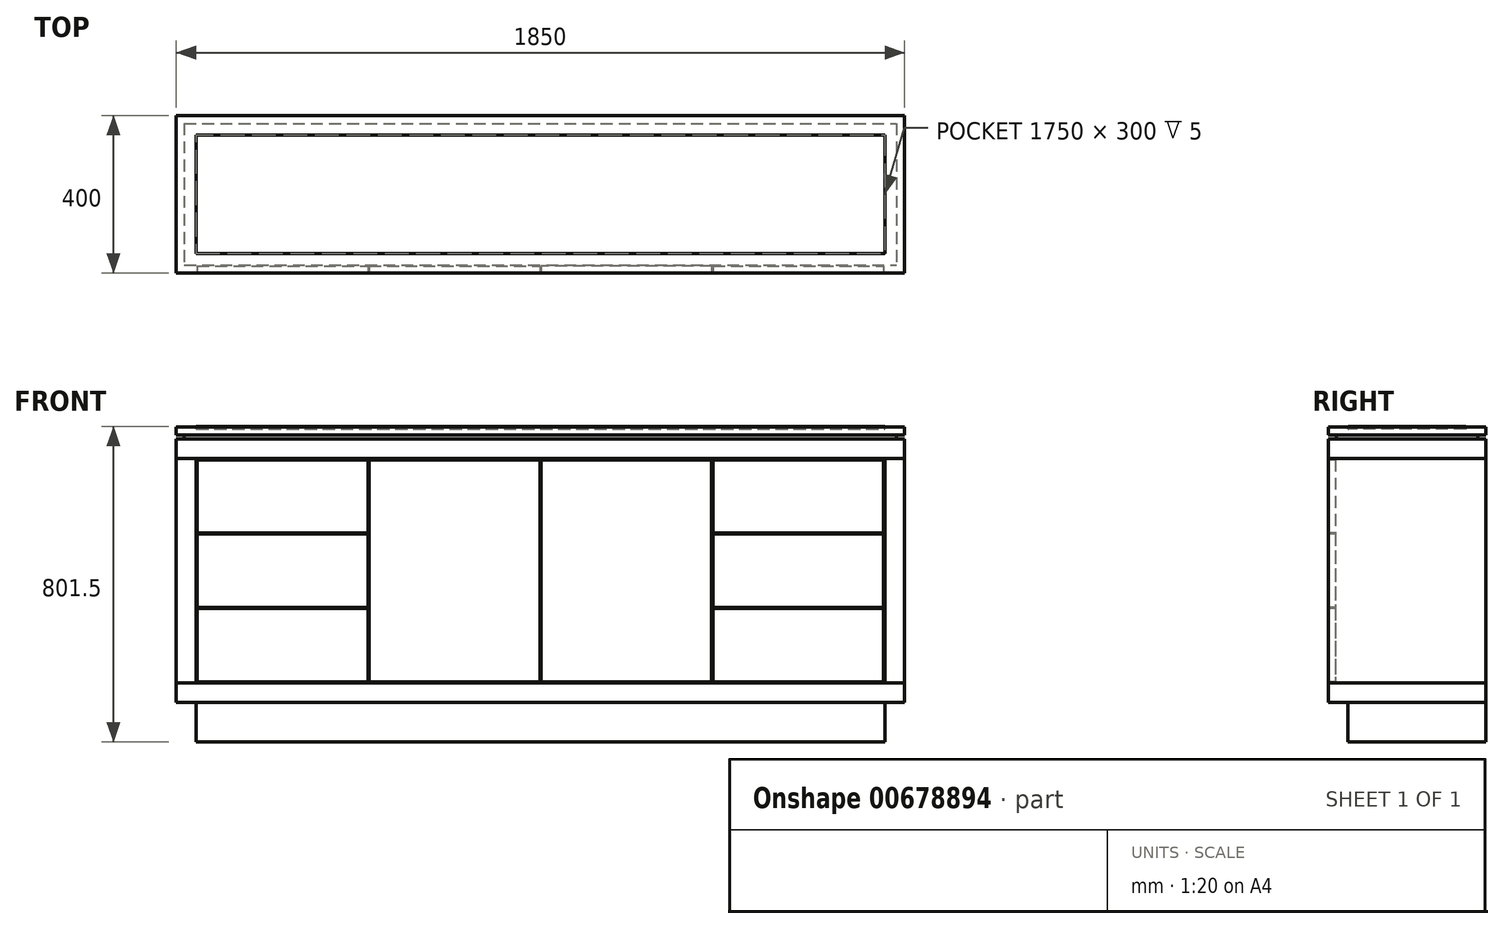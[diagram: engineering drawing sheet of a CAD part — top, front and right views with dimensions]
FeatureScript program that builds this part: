
annotation { "Feature Type Name" : "Feature", "Feature Type Description" : "" }
export const myFeature = defineFeature(function(context is Context, id is Id, definition is map)
    precondition{}
    {
        {
            var Q0;
            Q0=qCreatedBy(makeId("Front.planeOp"),FACE);
            var sketch = newSketch(context, id + "F0", { "sketchPlane" : qUnion([Q0])});
            skLineSegment(sketch, "E0.bottom", {"start": v(-925, 770) * mm, "end": v(925, 770) * mm});
            skLineSegment(sketch, "E0.top", {"start": v(-925, 100) * mm, "end": v(925, 100) * mm});
            skLineSegment(sketch, "E0.left", {"start": v(-925, 770) * mm, "end": v(-925, 100) * mm});
            skLineSegment(sketch, "E1.bottom", {"start": v(-925, 800) * mm, "end": v(925, 800) * mm});
            skLineSegment(sketch, "E1.top", {"start": v(-925, 780) * mm, "end": v(925, 780) * mm});
            skLineSegment(sketch, "E1.left", {"start": v(-925, 800) * mm, "end": v(-925, 780) * mm});
            skLineSegment(sketch, "E1.right", {"start": v(925, 800) * mm, "end": v(925, 780) * mm});
            skLineSegment(sketch, "E2", {"start": v(-875, 100) * mm, "end": v(-875, 0) * mm});
            skLineSegment(sketch, "E3", {"start": v(-875, 0) * mm, "end": v(875, 0) * mm});
            skLineSegment(sketch, "E4", {"start": v(875, 0) * mm, "end": v(875, 100) * mm});
            skLineSegment(sketch, "E5", {"start": v(905, 780) * mm, "end": v(905, 770) * mm});
            skLineSegment(sketch, "E6", {"start": v(925, 780) * mm, "end": v(925, 770) * mm, "construction": true});
            skLineSegment(sketch, "E7", {"start": v(-925, 780) * mm, "end": v(-925, 770) * mm, "construction": true});
            skLineSegment(sketch, "E8", {"start": v(-905, 770) * mm, "end": v(-905, 780) * mm});
            skLineSegment(sketch, "E9", {"start": v(925, 770) * mm, "end": v(925, 100) * mm});
            skLineSegment(sketch, "E10", {"start": v(925, 100) * mm, "end": v(925, 0) * mm, "construction": true});
            skLineSegment(sketch, "E11", {"start": v(925, 0) * mm, "end": v(875, 0) * mm, "construction": true});
            skLineSegment(sketch, "E12", {"start": v(-925, 100) * mm, "end": v(-925, 0) * mm, "construction": true});
            skLineSegment(sketch, "E13", {"start": v(-925, 0) * mm, "end": v(-875, 0) * mm, "construction": true});
            skLineSegment(sketch, "E14", {"start": v(-905, 775) * mm, "end": v(-925, 775) * mm, "construction": true});
            skLineSegment(sketch, "E15", {"start": v(925, 775) * mm, "end": v(905, 775) * mm, "construction": true});
            skLineSegment(sketch, "E16", {"start": v(-925, 720) * mm, "end": v(925, 720) * mm});
            skLineSegment(sketch, "E17", {"start": v(-925, 150) * mm, "end": v(925, 150) * mm});
            skLineSegment(sketch, "E18", {"start": v(-875, 100) * mm, "end": v(-875, 770) * mm});
            skLineSegment(sketch, "E19", {"start": v(875, 100) * mm, "end": v(875, 720) * mm});
            skLineSegment(sketch, "E20.bottom", {"start": v(-872, 528) * mm, "end": v(-438.25, 528) * mm});
            skLineSegment(sketch, "E20.top", {"start": v(-872, 153) * mm, "end": v(-438.25, 153) * mm});
            skLineSegment(sketch, "E20.left", {"start": v(-872, 528) * mm, "end": v(-872, 153) * mm});
            skLineSegment(sketch, "E20.right", {"start": v(-438.25, 528) * mm, "end": v(-438.25, 153) * mm});
            skLineSegment(sketch, "E21.bottom", {"start": v(-435.25, 528) * mm, "end": v(-1.5, 528) * mm});
            skLineSegment(sketch, "E21.top", {"start": v(-435.25, 153) * mm, "end": v(-1.5, 153) * mm});
            skLineSegment(sketch, "E21.left", {"start": v(-435.25, 528) * mm, "end": v(-435.25, 153) * mm});
            skLineSegment(sketch, "E21.right", {"start": v(-1.5, 528) * mm, "end": v(-1.5, 153) * mm});
            skLineSegment(sketch, "E22.bottom", {"start": v(1.5, 528) * mm, "end": v(435.25, 528) * mm});
            skLineSegment(sketch, "E22.top", {"start": v(1.5, 153) * mm, "end": v(435.25, 153) * mm});
            skLineSegment(sketch, "E22.left", {"start": v(1.5, 528) * mm, "end": v(1.5, 153) * mm});
            skLineSegment(sketch, "E22.right", {"start": v(435.25, 528) * mm, "end": v(435.25, 153) * mm});
            skLineSegment(sketch, "E23.bottom", {"start": v(438.25, 528) * mm, "end": v(872, 528) * mm});
            skLineSegment(sketch, "E23.top", {"start": v(438.25, 153) * mm, "end": v(872, 153) * mm});
            skLineSegment(sketch, "E23.left", {"start": v(438.25, 528) * mm, "end": v(438.25, 153) * mm});
            skLineSegment(sketch, "E23.right", {"start": v(872, 528) * mm, "end": v(872, 153) * mm});
            skLineSegment(sketch, "E24", {"start": v(-435.25, 153) * mm, "end": v(-438.25, 153) * mm, "construction": true});
            skLineSegment(sketch, "E25", {"start": v(-1.5, 153) * mm, "end": v(1.5, 153) * mm, "construction": true});
            skLineSegment(sketch, "E26", {"start": v(-872, 153) * mm, "end": v(-875, 153) * mm, "construction": true});
            skLineSegment(sketch, "E27", {"start": v(438.25, 153) * mm, "end": v(435.25, 153) * mm, "construction": true});
            skLineSegment(sketch, "E28", {"start": v(872, 153) * mm, "end": v(875, 153) * mm, "construction": true});
            skLineSegment(sketch, "E29", {"start": v(-872, 153) * mm, "end": v(-872, 150) * mm, "construction": true});
            skLineSegment(sketch, "E30", {"start": v(-655.12, 528) * mm, "end": v(-655.12, 531) * mm, "construction": true});
            skLineSegment(sketch, "E31", {"start": v(-655.12, 528) * mm, "end": v(-655.12, 340.5) * mm, "construction": true});
            skLineSegment(sketch, "E32", {"start": v(-655.12, 340.5) * mm, "end": v(-655.12, 153) * mm, "construction": true});
            skLineSegment(sketch, "E33", {"start": v(0, 532.5) * mm, "end": v(0, 720) * mm, "construction": true});
            skLineSegment(sketch, "E34", {"start": v(-435.25, 342) * mm, "end": v(435.25, 342) * mm});
            skLineSegment(sketch, "E35", {"start": v(435.25, 339) * mm, "end": v(-435.25, 339) * mm});
            skLineSegment(sketch, "E36", {"start": v(1.5, 528) * mm, "end": v(-1.5, 528) * mm, "construction": true});
            skLineSegment(sketch, "E37", {"start": v(0, 153) * mm, "end": v(0, 339) * mm, "construction": true});
            skLineSegment(sketch, "E38", {"start": v(0, 339) * mm, "end": v(0, 342) * mm, "construction": true});
            skLineSegment(sketch, "E39", {"start": v(0, 342) * mm, "end": v(0, 528) * mm, "construction": true});
            skLineSegment(sketch, "E40", {"start": v(-435.25, 342) * mm, "end": v(-872, 342) * mm});
            skLineSegment(sketch, "E41", {"start": v(-435.25, 339) * mm, "end": v(-872, 339) * mm});
            skLineSegment(sketch, "E42", {"start": v(435.25, 342) * mm, "end": v(872, 342) * mm});
            skLineSegment(sketch, "E43", {"start": v(435.25, 339) * mm, "end": v(872, 339) * mm});
            skPoint(sketch, "E44.endSnap0", {"position": v(0, 800) * mm});
            skLineSegment(sketch, "E45.bottom", {"start": v(-872, 717) * mm, "end": v(-438.25, 717) * mm});
            skLineSegment(sketch, "E45.top", {"start": v(-872, 531) * mm, "end": v(-438.25, 531) * mm});
            skLineSegment(sketch, "E45.left", {"start": v(-872, 717) * mm, "end": v(-872, 531) * mm});
            skLineSegment(sketch, "E45.right", {"start": v(-438.25, 717) * mm, "end": v(-438.25, 531) * mm});
            skLineSegment(sketch, "E46.bottom", {"start": v(-435.25, 717) * mm, "end": v(-1.5, 717) * mm});
            skLineSegment(sketch, "E46.top", {"start": v(-435.25, 531) * mm, "end": v(-1.5, 531) * mm});
            skLineSegment(sketch, "E46.left", {"start": v(-435.25, 717) * mm, "end": v(-435.25, 531) * mm});
            skLineSegment(sketch, "E46.right", {"start": v(-1.5, 717) * mm, "end": v(-1.5, 531) * mm});
            skLineSegment(sketch, "E47", {"start": v(-872, 531) * mm, "end": v(-872, 528) * mm});
            skLineSegment(sketch, "E48", {"start": v(-872, 717) * mm, "end": v(-872, 720) * mm});
            skLineSegment(sketch, "E49", {"start": v(-435.25, 531) * mm, "end": v(-435.25, 528) * mm});
            skLineSegment(sketch, "E50", {"start": v(-438.25, 717) * mm, "end": v(-435.25, 717) * mm});
            skLineSegment(sketch, "E51", {"start": v(-1.5, 531) * mm, "end": v(-1.5, 528) * mm});
            skSolve(sketch);
        }
        {
            var Q0;
            {var subQ5=sQuery(id+"F0.wireOp",EDGE,"E0.bottom");var subQ7=makeQuery(id+"F0.imprint","INTERSECT",VERTEX,{"derivedFrom":[subQ5,sQuery(id+"F0.wireOp",EDGE,"E5")]});Q0=makeQuery(id+"F0.imprint","IMPRINT",FACE,{"disambiguationData":[TD([[makeQuery(id+"F0.imprint","IMPRINT",EDGE,{"disambiguationData":[TD([[subQ7,1.0]])],"derivedFrom":subQ5}),-1.0]])]});}
            var Q1;
            {var subQ1=sQuery(id+"F0.wireOp",EDGE,"E0.left");var subQ5=sQuery(id+"F0.wireOp",EDGE,"E0.bottom");var subQ6=makeQuery(id+"F0.imprint","INTERSECT",VERTEX,{"derivedFrom":[subQ5,subQ1]});Q1=makeQuery(id+"F0.imprint","IMPRINT",FACE,{"disambiguationData":[TD([[makeQuery(id+"F0.imprint","IMPRINT",EDGE,{"disambiguationData":[TD([[subQ6,-1.0]])],"derivedFrom":subQ5}),-1.0]])]});}
            var Q2;
            {var subQ0=sQuery(id+"F0.wireOp",EDGE,"E0.left");var subQ1=sQuery(id+"F0.wireOp",EDGE,"E0.top");var subQ2=makeQuery(id+"F0.imprint","INTERSECT",VERTEX,{"derivedFrom":[subQ1,subQ0]});Q2=makeQuery(id+"F0.imprint","IMPRINT",FACE,{"disambiguationData":[TD([[makeQuery(id+"F0.imprint","IMPRINT",EDGE,{"disambiguationData":[TD([[subQ2,1.0]])],"derivedFrom":subQ0}),1.0]])]});}
            var Q3;
            {var subQ0=sQuery(id+"F0.wireOp",EDGE,"E18");var subQ5=sQuery(id+"F0.wireOp",EDGE,"E17");var subQ6=makeQuery(id+"F0.imprint","INTERSECT",VERTEX,{"derivedFrom":[subQ5,subQ0]});Q3=makeQuery(id+"F0.imprint","IMPRINT",FACE,{"disambiguationData":[TD([[makeQuery(id+"F0.imprint","IMPRINT",EDGE,{"disambiguationData":[TD([[subQ6,-1.0]])],"derivedFrom":subQ5}),-1.0]])]});}
            var Q4;
            {var subQ0=sQuery(id+"F0.wireOp",EDGE,"E9");var subQ1=sQuery(id+"F0.wireOp",EDGE,"E0.top");var subQ2=makeQuery(id+"F0.imprint","INTERSECT",VERTEX,{"derivedFrom":[subQ1,subQ0]});Q4=makeQuery(id+"F0.imprint","IMPRINT",FACE,{"disambiguationData":[TD([[makeQuery(id+"F0.imprint","IMPRINT",EDGE,{"disambiguationData":[TD([[subQ2,1.0]])],"derivedFrom":subQ0}),-1.0]])]});}
            var Q5;
            Q5=makeQuery(id+"F0.imprint","IMPRINT",FACE,{"disambiguationData":[TD([[makeQuery(id+"F0.imprint","IMPRINT",EDGE,{"derivedFrom":sQuery(id+"F0.wireOp",EDGE,"5v0JZrxY-nqoR-NWn2-a046-kkwBJGH1RzHE.bottom")}),-1.0]])]});
            extrude(context, id + "F1", {"entities" : qUnion([Q0, Q1, Q2, Q3, Q4, Q5]), "oppositeDirection" : true, "depth" : 400 * mm, "offsetDistance" : 25 * mm});
        }
        {
            var Q0;
            {var subQ0=sQuery(id+"F0.wireOp",EDGE,"5v0JZrxY-nqoR-NWn2-a046-kkwBJGH1RzHE.left");Q0=makeQuery(id+"F0.imprint","IMPRINT",FACE,{"disambiguationData":[TD([[makeQuery(id+"F0.imprint","IMPRINT",EDGE,{"derivedFrom":subQ0}),-1.0]])]});}
            var Q1;
            {var subQ0=sQuery(id+"F0.wireOp",EDGE,"5v0JZrxY-nqoR-NWn2-a046-kkwBJGH1RzHE.right");Q1=makeQuery(id+"F0.imprint","IMPRINT",FACE,{"disambiguationData":[TD([[makeQuery(id+"F0.imprint","IMPRINT",EDGE,{"derivedFrom":subQ0}),1.0]])]});}
            var Q2;
            {var subQ0=sQuery(id+"F0.wireOp",EDGE,"E16");var subQ1=sQuery(id+"F0.wireOp",EDGE,"E0.left");var subQ2=makeQuery(id+"F0.imprint","INTERSECT",VERTEX,{"derivedFrom":[subQ1,subQ0]});Q2=makeQuery(id+"F0.imprint","IMPRINT",FACE,{"disambiguationData":[TD([[makeQuery(id+"F0.imprint","IMPRINT",EDGE,{"disambiguationData":[TD([[subQ2,-1.0]])],"derivedFrom":subQ1}),1.0]])]});}
            var Q3;
            {var subQ0=sQuery(id+"F0.wireOp",EDGE,"E16");var subQ1=sQuery(id+"F0.wireOp",EDGE,"E9");var subQ2=makeQuery(id+"F0.imprint","INTERSECT",VERTEX,{"derivedFrom":[subQ1,subQ0]});Q3=makeQuery(id+"F0.imprint","IMPRINT",FACE,{"disambiguationData":[TD([[makeQuery(id+"F0.imprint","IMPRINT",EDGE,{"disambiguationData":[TD([[subQ2,-1.0]])],"derivedFrom":subQ1}),-1.0]])]});}
            extrude(context, id + "F2", {"entities" : qUnion([Q0, Q1, Q2, Q3]), "oppositeDirection" : true, "depth" : 400 * mm, "offsetDistance" : 25 * mm});
        }
        {
            var Q0;
            {var subQ0=sQuery(id+"F0.wireOp",EDGE,"E2");Q0=makeQuery(id+"F0.imprint","IMPRINT",FACE,{"disambiguationData":[TD([[makeQuery(id+"F0.imprint","IMPRINT",EDGE,{"derivedFrom":subQ0}),1.0]])]});}
            extrude(context, id + "F3", {"entities" : qUnion([Q0]), "oppositeDirection" : true, "depth" : 400 * mm, "offsetDistance" : 25 * mm, "hasSecondDirection" : true, "secondDirectionOppositeDirection" : true, "secondDirectionDepth" : 50 * mm});
        }
        {
            var Q0;
            {var subQ0=sQuery(id+"F0.wireOp",EDGE,"E20.bottom");Q0=makeQuery(id+"F0.imprint","IMPRINT",FACE,{"disambiguationData":[TD([[makeQuery(id+"F0.imprint","IMPRINT",EDGE,{"derivedFrom":subQ0}),-1.0]])]});}
            var Q1;
            {var subQ0=sQuery(id+"F0.wireOp",EDGE,"E20.top");Q1=makeQuery(id+"F0.imprint","IMPRINT",FACE,{"disambiguationData":[TD([[makeQuery(id+"F0.imprint","IMPRINT",EDGE,{"derivedFrom":subQ0}),1.0]])]});}
            var Q2;
            {var subQ0=sQuery(id+"F0.wireOp",EDGE,"E21.bottom");Q2=makeQuery(id+"F0.imprint","IMPRINT",FACE,{"disambiguationData":[TD([[makeQuery(id+"F0.imprint","IMPRINT",EDGE,{"derivedFrom":subQ0}),-1.0]])]});}
            var Q3;
            {var subQ0=sQuery(id+"F0.wireOp",EDGE,"E21.top");Q3=makeQuery(id+"F0.imprint","IMPRINT",FACE,{"disambiguationData":[TD([[makeQuery(id+"F0.imprint","IMPRINT",EDGE,{"derivedFrom":subQ0}),1.0]])]});}
            var Q4;
            {var subQ0=sQuery(id+"F0.wireOp",EDGE,"E34");var subQ5=sQuery(id+"F0.wireOp",EDGE,"E21.right");var subQ6=makeQuery(id+"F0.imprint","INTERSECT",VERTEX,{"derivedFrom":[subQ5,subQ0]});Q4=makeQuery(id+"F0.imprint","IMPRINT",FACE,{"disambiguationData":[TD([[makeQuery(id+"F0.imprint","IMPRINT",EDGE,{"disambiguationData":[TD([[subQ6,-1.0]])],"derivedFrom":subQ5}),-1.0]])]});}
            var Q5;
            Q5=makeQuery(id+"F0.imprint","IMPRINT",FACE,{"disambiguationData":[TD([[makeQuery(id+"F0.imprint","IMPRINT",EDGE,{"derivedFrom":sQuery(id+"F0.wireOp",EDGE,"E45.bottom")}),-1.0]])]});
            var Q6;
            Q6=makeQuery(id+"F0.imprint","IMPRINT",FACE,{"disambiguationData":[TD([[makeQuery(id+"F0.imprint","IMPRINT",EDGE,{"derivedFrom":sQuery(id+"F0.wireOp",EDGE,"E46.bottom")}),-1.0]])]});
            var Q7;
            Q7=makeQuery(id+"F0.imprint","IMPRINT",FACE,{"disambiguationData":[TD([[makeQuery(id+"F0.imprint","IMPRINT",EDGE,{"derivedFrom":sQuery(id+"F0.wireOp",EDGE,"E21.bottom")}),1.0]])]});
            extrude(context, id + "F4", {"entities" : qUnion([Q0, Q1, Q2, Q3, Q4, Q5, Q6, Q7]), "oppositeDirection" : true, "depth" : 18 * mm, "offsetDistance" : 25 * mm});
        }
        {
            var Q0;
            {var subQ0=sQuery(id+"F0.wireOp",EDGE,"E5");Q0=makeQuery(id+"F0.imprint","IMPRINT",FACE,{"disambiguationData":[TD([[makeQuery(id+"F0.imprint","IMPRINT",EDGE,{"derivedFrom":subQ0}),-1.0]])]});}
            extrude(context, id + "F5", {"entities" : qUnion([Q0]), "oppositeDirection" : true, "depth" : 380 * mm, "offsetDistance" : 25 * mm, "hasSecondDirection" : true, "secondDirectionOppositeDirection" : true, "secondDirectionDepth" : 20 * mm});
        }
        {
            var Q0;
            Q0=makeQuery(id+"F0.imprint","IMPRINT",FACE,{"disambiguationData":[TD([[makeQuery(id+"F0.imprint","IMPRINT",EDGE,{"derivedFrom":sQuery(id+"F0.wireOp",EDGE,"E1.bottom")}),-1.0]])]});
            extrude(context, id + "F6", {"entities" : qUnion([Q0]), "oppositeDirection" : true, "depth" : 400 * mm, "offsetDistance" : 25 * mm});
        }
        {
            var Q0;
            Q0=makeQuery(id+"F4.opExtrude","SWEPT_FACE",FACE,{"disambiguationData":[OSD([sQuery(id+"F0.wireOp",EDGE,"E21.right"),sQuery(id+"F0.wireOp",EDGE,"E46.right"),sQuery(id+"F0.wireOp",EDGE,"E51")])]});
            cPlane(context, id + "F7", {"entities" : qUnion([Q0]), "cplaneType" : CPlaneType.OFFSET, "offset" : 1.5 * mm, "width" : 150 * mm, "height" : 150 * mm});
        }
        {
            var Q0;
            Q0=makeQuery(id+"F4.opExtrude","SWEPT_BODY",BODY,{"disambiguationData":[OSD([sQuery(id+"F0.wireOp",EDGE,"E45.bottom"),sQuery(id+"F0.wireOp",EDGE,"E45.top"),sQuery(id+"F0.wireOp",EDGE,"E45.left"),sQuery(id+"F0.wireOp",EDGE,"E45.right")])]});
            var Q1;
            Q1=makeQuery(id+"F4.opExtrude","SWEPT_BODY",BODY,{"disambiguationData":[OSD([sQuery(id+"F0.wireOp",EDGE,"E20.bottom"),sQuery(id+"F0.wireOp",EDGE,"E20.left"),sQuery(id+"F0.wireOp",EDGE,"E20.right"),sQuery(id+"F0.wireOp",EDGE,"E40")])]});
            var Q2;
            Q2=makeQuery(id+"F4.opExtrude","SWEPT_BODY",BODY,{"disambiguationData":[OSD([sQuery(id+"F0.wireOp",EDGE,"E20.top"),sQuery(id+"F0.wireOp",EDGE,"E20.left"),sQuery(id+"F0.wireOp",EDGE,"E20.right"),sQuery(id+"F0.wireOp",EDGE,"E41")])]});
            var Q3;
            Q3=makeQuery(id+"F4.opExtrude","SWEPT_BODY",BODY,{"disambiguationData":[OSD([sQuery(id+"F0.wireOp",EDGE,"E21.top"),sQuery(id+"F0.wireOp",EDGE,"E21.left"),sQuery(id+"F0.wireOp",EDGE,"E21.right"),sQuery(id+"F0.wireOp",EDGE,"E46.bottom"),sQuery(id+"F0.wireOp",EDGE,"E46.left"),sQuery(id+"F0.wireOp",EDGE,"E46.right"),sQuery(id+"F0.wireOp",EDGE,"E49"),sQuery(id+"F0.wireOp",EDGE,"E51")])]});
            var Q4;
            Q4=qCreatedBy(id+"F7.planeOp",FACE);
            mirror(context, id + "F8", {"entities" : qUnion([Q0, Q1, Q2, Q3]), "mirrorPlane" : qUnion([Q4])});
        }
        {
            var Q0;
            Q0=makeQuery(id+"F6.opExtrude","SWEPT_FACE",FACE,{"disambiguationData":[OSD([sQuery(id+"F0.wireOp",EDGE,"E1.bottom")])]});
            var sketch = newSketch(context, id + "F9", { "sketchPlane" : qUnion([Q0])});
            skLineSegment(sketch, "E52.bottom", {"start": v(-875, 350) * mm, "end": v(875, 350) * mm});
            skLineSegment(sketch, "E52.top", {"start": v(-875, 50) * mm, "end": v(875, 50) * mm});
            skLineSegment(sketch, "E52.left", {"start": v(-875, 350) * mm, "end": v(-875, 50) * mm});
            skLineSegment(sketch, "E52.right", {"start": v(875, 350) * mm, "end": v(875, 50) * mm});
            skSolve(sketch);
        }
        {
            var Q0;
            Q0=makeQuery(id+"F9.imprint","IMPRINT",FACE,{"disambiguationData":[TD([[makeQuery(id+"F9.imprint","IMPRINT",EDGE,{"derivedFrom":sQuery(id+"F9.wireOp",EDGE,"E52.bottom")}),-1.0]])]});
            extrude(context, id + "F10", {"entities" : qUnion([Q0]), "operationType" : NewBodyOperationType.REMOVE, "oppositeDirection" : true, "depth" : 5 * mm, "offsetDistance" : 25 * mm});
        }
        {
            var Q0;
            Q0=makeQuery(id+"F10.boolean.opBoolean","COPY",FACE,{"derivedFrom":makeQuery(id+"F10.opExtrude","CAP_FACE",FACE,{"disambiguationData":[OSD([sQuery(id+"F9.wireOp",EDGE,"E52.bottom"),sQuery(id+"F9.wireOp",EDGE,"E52.top"),sQuery(id+"F9.wireOp",EDGE,"E52.left"),sQuery(id+"F9.wireOp",EDGE,"E52.right")])],"isStart":false})});
            extrude(context, id + "F11", {"entities" : qUnion([Q0]), "depth" : 6.5 * mm, "offsetDistance" : 25 * mm});
        }
        {
            var Q0;
            Q0=makeQuery(id+"F11.opExtrude","CAP_FACE",FACE,{"disambiguationData":[OSD([sQuery(id+"F9.wireOp",EDGE,"E52.bottom"),sQuery(id+"F9.wireOp",EDGE,"E52.top"),sQuery(id+"F9.wireOp",EDGE,"E52.left"),sQuery(id+"F9.wireOp",EDGE,"E52.right")])],"isStart":false});
            var Q1;
            Q1=makeQuery(id+"F11.opExtrude","SWEPT_EDGE",EDGE,{"disambiguationData":[OSD([sQuery(id+"F9.wireOp",EDGE,"E52.top"),sQuery(id+"F9.wireOp",EDGE,"E52.left")])]});
            var Q2;
            Q2=makeQuery(id+"F11.opExtrude","SWEPT_EDGE",EDGE,{"disambiguationData":[OSD([sQuery(id+"F9.wireOp",EDGE,"E52.bottom"),sQuery(id+"F9.wireOp",EDGE,"E52.left")])]});
            var Q3;
            Q3=makeQuery(id+"F11.opExtrude","SWEPT_EDGE",EDGE,{"disambiguationData":[OSD([sQuery(id+"F9.wireOp",EDGE,"E52.bottom"),sQuery(id+"F9.wireOp",EDGE,"E52.right")])]});
            var Q4;
            Q4=makeQuery(id+"F11.opExtrude","SWEPT_EDGE",EDGE,{"disambiguationData":[OSD([sQuery(id+"F9.wireOp",EDGE,"E52.top"),sQuery(id+"F9.wireOp",EDGE,"E52.right")])]});
            fillet(context, id + "F12", {"entities" : qUnion([Q0, Q1, Q2, Q3, Q4]), "radius" : 1.5 * mm, "tangentPropagation" : true, "allowEdgeOverflow" : false});
        }
    });
